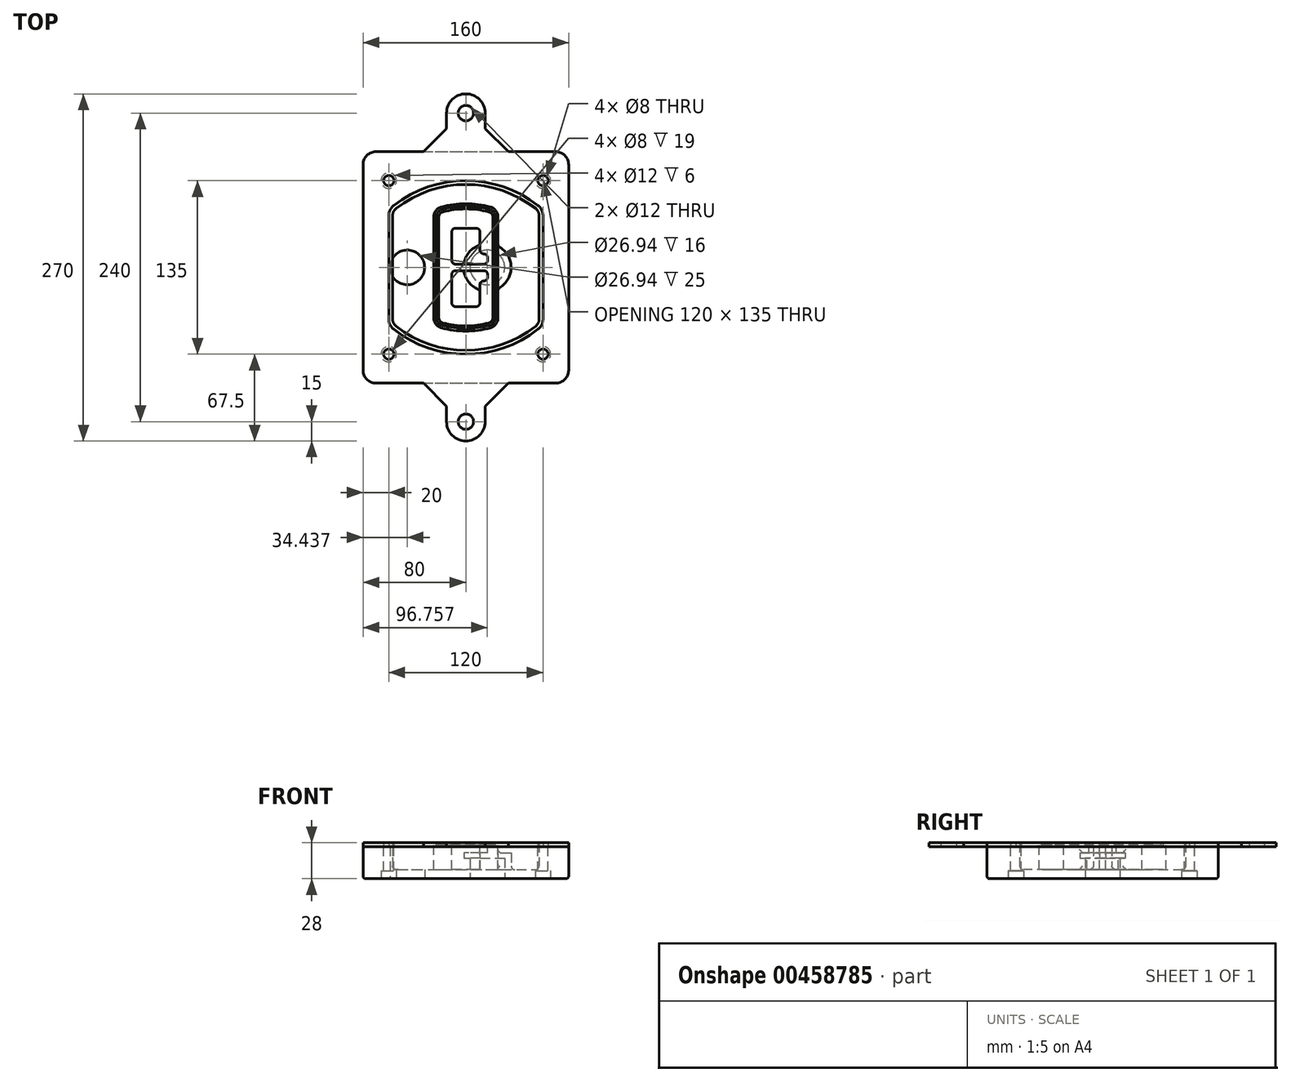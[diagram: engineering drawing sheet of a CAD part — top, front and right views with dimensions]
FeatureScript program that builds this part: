
annotation { "Feature Type Name" : "Feature", "Feature Type Description" : "" }
export const myFeature = defineFeature(function(context is Context, id is Id, definition is map)
    precondition{}
    {
        {
            var Q0;
            Q0=qCreatedBy(makeId("Top.planeOp"),FACE);
            var sketch = newSketch(context, id + "F0", { "sketchPlane" : qUnion([Q0])});
            skPoint(sketch, "E0.rect.middle", {"position": v(0, 0) * mm});
            skLineSegment(sketch, "E1.bottom", {"start": v(-70, -90) * mm, "end": v(70, -90) * mm});
            skLineSegment(sketch, "E1.top", {"start": v(-70, 90) * mm, "end": v(70, 90) * mm});
            skLineSegment(sketch, "E1.left", {"start": v(-80, -80) * mm, "end": v(-80, 80) * mm});
            skLineSegment(sketch, "E1.right", {"start": v(80, -80) * mm, "end": v(80, 80) * mm});
            skLineSegment(sketch, "E2", {"start": v(-80, 90) * mm, "end": v(80, -90) * mm, "construction": true});
            skLineSegment(sketch, "E3", {"start": v(80, 90) * mm, "end": v(-80, -90) * mm, "construction": true});
            skCircle(sketch, "E4", {"center": v(-60, 67.5) * mm, "radius": 4 * mm});
            skCircle(sketch, "E5", {"center": v(60, 67.5) * mm, "radius": 4 * mm});
            skCircle(sketch, "E6", {"center": v(60, -67.5) * mm, "radius": 4 * mm});
            skCircle(sketch, "E7", {"center": v(-60, -67.5) * mm, "radius": 4 * mm});
            skLineSegment(sketch, "E8", {"start": v(-60, 67.5) * mm, "end": v(60, 67.5) * mm, "construction": true});
            skLineSegment(sketch, "E9", {"start": v(60, 67.5) * mm, "end": v(60, -67.5) * mm, "construction": true});
            skLineSegment(sketch, "E10", {"start": v(60, -67.5) * mm, "end": v(-60, -67.5) * mm, "construction": true});
            skLineSegment(sketch, "E11", {"start": v(-60, -67.5) * mm, "end": v(-60, 67.5) * mm, "construction": true});
            skLineSegment(sketch, "E12", {"start": v(-60, 40.3) * mm, "end": v(-60, -40.3) * mm});
            skLineSegment(sketch, "E13", {"start": v(60, 40.3) * mm, "end": v(60, -40.3) * mm});
            skArc(sketch, "E14", {"start": v(56.15, 48.18) * mm, "mid": v(0, 67.5) * mm, "end": v(-56.15, 48.18) * mm});
            skArc(sketch, "E15", {"start": v(-56.15, -48.18) * mm, "mid": v(0, -67.5) * mm, "end": v(56.15, -48.18) * mm});
            skLineSegment(sketch, "E16", {"start": v(-60, 0) * mm, "end": v(60, 0) * mm, "construction": true});
            skPoint(sketch, "E17.visualSharp", {"position": v(-60, -45) * mm});
            skArc(sketch, "E17.filletArc", {"start": v(-60, -40.3) * mm, "mid": v(-58.99, -44.68) * mm, "end": v(-56.15, -48.18) * mm});
            skPoint(sketch, "E18.visualSharp", {"position": v(-60, 45) * mm});
            skArc(sketch, "E18.filletArc", {"start": v(-56.15, 48.18) * mm, "mid": v(-58.99, 44.68) * mm, "end": v(-60, 40.3) * mm});
            skPoint(sketch, "E19.visualSharp", {"position": v(60, 45) * mm});
            skArc(sketch, "E19.filletArc", {"start": v(60, 40.3) * mm, "mid": v(58.99, 44.68) * mm, "end": v(56.15, 48.18) * mm});
            skPoint(sketch, "E20.visualSharp", {"position": v(60, -45) * mm});
            skArc(sketch, "E20.filletArc", {"start": v(56.15, -48.18) * mm, "mid": v(58.99, -44.68) * mm, "end": v(60, -40.3) * mm});
            skPoint(sketch, "E21.visualSharp", {"position": v(-80, 90) * mm});
            skArc(sketch, "E21.filletArc", {"start": v(-70, 90) * mm, "mid": v(-77.07, 87.07) * mm, "end": v(-80, 80) * mm});
            skPoint(sketch, "E22.visualSharp", {"position": v(80, 90) * mm});
            skArc(sketch, "E22.filletArc", {"start": v(80, 80) * mm, "mid": v(77.07, 87.07) * mm, "end": v(70, 90) * mm});
            skPoint(sketch, "E23.visualSharp", {"position": v(80, -90) * mm});
            skArc(sketch, "E23.filletArc", {"start": v(70, -90) * mm, "mid": v(77.07, -87.07) * mm, "end": v(80, -80) * mm});
            skPoint(sketch, "E24.visualSharp", {"position": v(-80, -90) * mm});
            skArc(sketch, "E24.filletArc", {"start": v(-80, -80) * mm, "mid": v(-77.07, -87.07) * mm, "end": v(-70, -90) * mm});
            skArc(sketch, "E25.0", {"start": v(57, 40.3) * mm, "mid": v(56.3, 43.36) * mm, "end": v(54.3, 45.81) * mm});
            skLineSegment(sketch, "E25.1", {"start": v(57, 40.3) * mm, "end": v(57, -40.3) * mm});
            skArc(sketch, "E25.2", {"start": v(54.3, -45.81) * mm, "mid": v(56.3, -43.36) * mm, "end": v(57, -40.3) * mm});
            skArc(sketch, "E25.3", {"start": v(-54.3, -45.81) * mm, "mid": v(0, -64.5) * mm, "end": v(54.3, -45.81) * mm});
            skArc(sketch, "E25.4", {"start": v(-57, -40.3) * mm, "mid": v(-56.3, -43.36) * mm, "end": v(-54.3, -45.81) * mm});
            skArc(sketch, "E25.5", {"start": v(54.3, 45.81) * mm, "mid": v(0, 64.5) * mm, "end": v(-54.3, 45.81) * mm});
            skLineSegment(sketch, "E25.6", {"start": v(-57, 40.3) * mm, "end": v(-57, -40.3) * mm});
            skArc(sketch, "E25.7", {"start": v(-54.3, 45.81) * mm, "mid": v(-56.3, 43.36) * mm, "end": v(-57, 40.3) * mm});
            skArc(sketch, "E26.0", {"start": v(-58.62, 51.33) * mm, "mid": v(-62.58, 46.43) * mm, "end": v(-64, 40.3) * mm});
            skArc(sketch, "E26.1", {"start": v(58.62, 51.33) * mm, "mid": v(0, 71.5) * mm, "end": v(-58.62, 51.33) * mm});
            skArc(sketch, "E26.2", {"start": v(64, 40.3) * mm, "mid": v(62.58, 46.43) * mm, "end": v(58.62, 51.33) * mm});
            skLineSegment(sketch, "E26.3", {"start": v(64, 40.3) * mm, "end": v(64, -40.3) * mm});
            skArc(sketch, "E26.4", {"start": v(58.62, -51.33) * mm, "mid": v(62.58, -46.43) * mm, "end": v(64, -40.3) * mm});
            skLineSegment(sketch, "E26.5", {"start": v(-64, 40.3) * mm, "end": v(-64, -40.3) * mm});
            skArc(sketch, "E26.6", {"start": v(-58.62, -51.33) * mm, "mid": v(0, -71.5) * mm, "end": v(58.62, -51.33) * mm});
            skArc(sketch, "E26.7", {"start": v(-64, -40.3) * mm, "mid": v(-62.58, -46.43) * mm, "end": v(-58.62, -51.33) * mm});
            skSolve(sketch);
        }
        {
            var Q0;
            Q0=makeQuery(id+"F0.imprint","IMPRINT",FACE,{"disambiguationData":[TD([[makeQuery(id+"F0.imprint","IMPRINT",EDGE,{"derivedFrom":sQuery(id+"F0.wireOp",EDGE,"E1.bottom")}),1.0]])]});
            var Q1;
            Q1=makeQuery(id+"F0.imprint","IMPRINT",FACE,{"disambiguationData":[TD([[makeQuery(id+"F0.imprint","IMPRINT",EDGE,{"derivedFrom":sQuery(id+"F0.wireOp",EDGE,"E12")}),1.0]])]});
            var Q2;
            Q2=makeQuery(id+"F0.imprint","IMPRINT",FACE,{"disambiguationData":[TD([[makeQuery(id+"F0.imprint","IMPRINT",EDGE,{"derivedFrom":sQuery(id+"F0.wireOp",EDGE,"E25.0")}),1.0]])]});
            var Q3;
            Q3=makeQuery(id+"F0.imprint","IMPRINT",FACE,{"disambiguationData":[TD([[makeQuery(id+"F0.imprint","IMPRINT",EDGE,{"derivedFrom":sQuery(id+"F0.wireOp",EDGE,"E12")}),-1.0]])]});
            extrude(context, id + "F1", {"entities" : qUnion([Q0, Q1, Q2, Q3]), "oppositeDirection" : true, "depth" : 25 * mm});
        }
        {
            var Q0;
            Q0=makeQuery(id+"F0.imprint","IMPRINT",FACE,{"disambiguationData":[TD([[makeQuery(id+"F0.imprint","IMPRINT",EDGE,{"derivedFrom":sQuery(id+"F0.wireOp",EDGE,"E12")}),1.0]])]});
            extrude(context, id + "F2", {"entities" : qUnion([Q0]), "operationType" : NewBodyOperationType.ADD, "depth" : 3 * mm});
        }
        {
            var Q0;
            Q0=makeQuery(id+"F0.imprint","IMPRINT",FACE,{"disambiguationData":[TD([[makeQuery(id+"F0.imprint","IMPRINT",EDGE,{"derivedFrom":sQuery(id+"F0.wireOp",EDGE,"E25.0")}),1.0]])]});
            extrude(context, id + "F3", {"entities" : qUnion([Q0]), "operationType" : NewBodyOperationType.REMOVE, "oppositeDirection" : true, "depth" : 18 * mm});
        }
        {
            var Q0;
            Q0=makeQuery(id+"F2.opExtrude","CAP_FACE",FACE,{"disambiguationData":[OSD([sQuery(id+"F0.wireOp",EDGE,"E12"),sQuery(id+"F0.wireOp",EDGE,"E13"),sQuery(id+"F0.wireOp",EDGE,"E14"),sQuery(id+"F0.wireOp",EDGE,"E15"),sQuery(id+"F0.wireOp",EDGE,"E17.filletArc"),sQuery(id+"F0.wireOp",EDGE,"E18.filletArc"),sQuery(id+"F0.wireOp",EDGE,"E19.filletArc"),sQuery(id+"F0.wireOp",EDGE,"E20.filletArc"),sQuery(id+"F0.wireOp",EDGE,"E25.0"),sQuery(id+"F0.wireOp",EDGE,"E25.1"),sQuery(id+"F0.wireOp",EDGE,"E25.2"),sQuery(id+"F0.wireOp",EDGE,"E25.3"),sQuery(id+"F0.wireOp",EDGE,"E25.4"),sQuery(id+"F0.wireOp",EDGE,"E25.5"),sQuery(id+"F0.wireOp",EDGE,"E25.6"),sQuery(id+"F0.wireOp",EDGE,"E25.7")])],"isStart":false});
            var sketch = newSketch(context, id + "F4", { "sketchPlane" : qUnion([Q0])});
            skArc(sketch, "E27.0", {"start": v(-19.08, -46.97) * mm, "mid": v(0, -49.5) * mm, "end": v(19.08, -46.97) * mm});
            skArc(sketch, "E28.0", {"start": v(19.08, 46.97) * mm, "mid": v(0, 49.5) * mm, "end": v(-19.08, 46.97) * mm});
            skLineSegment(sketch, "E29", {"start": v(-25, 39.25) * mm, "end": v(-25, -39.25) * mm});
            skLineSegment(sketch, "E30", {"start": v(25, 39.25) * mm, "end": v(25, -39.25) * mm});
            skLineSegment(sketch, "E31", {"start": v(-25, 45.1) * mm, "end": v(25, 45.1) * mm, "construction": true});
            skLineSegment(sketch, "E32", {"start": v(-25, -45.1) * mm, "end": v(25, -45.1) * mm, "construction": true});
            skPoint(sketch, "E33.visualSharp", {"position": v(-25, 45.1) * mm});
            skArc(sketch, "E33.filletArc", {"start": v(-19.08, 46.97) * mm, "mid": v(-23.35, 44.11) * mm, "end": v(-25, 39.25) * mm});
            skPoint(sketch, "E34.visualSharp", {"position": v(25, 45.1) * mm});
            skArc(sketch, "E34.filletArc", {"start": v(25, 39.25) * mm, "mid": v(23.35, 44.11) * mm, "end": v(19.08, 46.97) * mm});
            skPoint(sketch, "E35.visualSharp", {"position": v(25, -45.1) * mm});
            skArc(sketch, "E35.filletArc", {"start": v(19.08, -46.97) * mm, "mid": v(23.35, -44.11) * mm, "end": v(25, -39.25) * mm});
            skPoint(sketch, "E36.visualSharp", {"position": v(-25, -45.1) * mm});
            skArc(sketch, "E36.filletArc", {"start": v(-25, -39.25) * mm, "mid": v(-23.35, -44.11) * mm, "end": v(-19.08, -46.97) * mm});
            skArc(sketch, "E37.0", {"start": v(54.3, 45.81) * mm, "mid": v(0, 64.5) * mm, "end": v(-54.3, 45.81) * mm});
            skArc(sketch, "E37.1", {"start": v(-54.3, 45.81) * mm, "mid": v(-56.3, 43.36) * mm, "end": v(-57, 40.3) * mm});
            skLineSegment(sketch, "E37.2", {"start": v(-57, 40.3) * mm, "end": v(-57, -40.3) * mm});
            skArc(sketch, "E37.3", {"start": v(-57, -40.3) * mm, "mid": v(-56.3, -43.36) * mm, "end": v(-54.3, -45.81) * mm});
            skArc(sketch, "E37.4", {"start": v(-54.3, -45.81) * mm, "mid": v(0, -64.5) * mm, "end": v(54.3, -45.81) * mm});
            skArc(sketch, "E37.5", {"start": v(54.3, -45.81) * mm, "mid": v(56.3, -43.36) * mm, "end": v(57, -40.3) * mm});
            skLineSegment(sketch, "E37.6", {"start": v(57, 40.3) * mm, "end": v(57, -40.3) * mm});
            skArc(sketch, "E37.7", {"start": v(57, 40.3) * mm, "mid": v(56.3, 43.36) * mm, "end": v(54.3, 45.81) * mm});
            skLineSegment(sketch, "E38.0", {"start": v(23, 39.25) * mm, "end": v(23, -39.25) * mm});
            skArc(sketch, "E38.1", {"start": v(18.56, -45.04) * mm, "mid": v(21.76, -42.9) * mm, "end": v(23, -39.25) * mm});
            skArc(sketch, "E38.2", {"start": v(-18.56, -45.04) * mm, "mid": v(0, -47.5) * mm, "end": v(18.56, -45.04) * mm});
            skArc(sketch, "E38.3", {"start": v(-23, -39.25) * mm, "mid": v(-21.76, -42.9) * mm, "end": v(-18.56, -45.04) * mm});
            skLineSegment(sketch, "E38.4", {"start": v(-23, 39.25) * mm, "end": v(-23, -39.25) * mm});
            skArc(sketch, "E38.5", {"start": v(23, 39.25) * mm, "mid": v(21.76, 42.9) * mm, "end": v(18.56, 45.04) * mm});
            skArc(sketch, "E38.6", {"start": v(-18.56, 45.04) * mm, "mid": v(-21.76, 42.9) * mm, "end": v(-23, 39.25) * mm});
            skArc(sketch, "E38.7", {"start": v(18.56, 45.04) * mm, "mid": v(0, 47.5) * mm, "end": v(-18.56, 45.04) * mm});
            skArc(sketch, "E39.0", {"start": v(21, 39.25) * mm, "mid": v(20.18, 41.68) * mm, "end": v(18.04, 43.1) * mm});
            skLineSegment(sketch, "E39.1", {"start": v(21, 39.25) * mm, "end": v(21, -39.25) * mm});
            skArc(sketch, "E39.2", {"start": v(18.04, -43.1) * mm, "mid": v(20.18, -41.68) * mm, "end": v(21, -39.25) * mm});
            skArc(sketch, "E39.3", {"start": v(-18.04, -43.1) * mm, "mid": v(0, -45.5) * mm, "end": v(18.04, -43.1) * mm});
            skArc(sketch, "E39.4", {"start": v(-21, -39.25) * mm, "mid": v(-20.18, -41.68) * mm, "end": v(-18.04, -43.1) * mm});
            skArc(sketch, "E39.5", {"start": v(18.04, 43.1) * mm, "mid": v(0, 45.5) * mm, "end": v(-18.04, 43.1) * mm});
            skLineSegment(sketch, "E39.6", {"start": v(-21, 39.25) * mm, "end": v(-21, -39.25) * mm});
            skArc(sketch, "E39.7", {"start": v(-18.04, 43.1) * mm, "mid": v(-20.18, 41.68) * mm, "end": v(-21, 39.25) * mm});
            skLineSegment(sketch, "E40", {"start": v(-25, 0) * mm, "end": v(25, 0) * mm, "construction": true});
            skLineSegment(sketch, "E41", {"start": v(-11, 5.5) * mm, "end": v(-11, 27.5) * mm});
            skLineSegment(sketch, "E42", {"start": v(-8, 30.5) * mm, "end": v(8, 30.5) * mm});
            skLineSegment(sketch, "E43", {"start": v(11, 27.5) * mm, "end": v(11, 13.5) * mm});
            skLineSegment(sketch, "E44", {"start": v(14, 10.5) * mm, "end": v(14, 10.5) * mm});
            skLineSegment(sketch, "E45", {"start": v(17, 7.5) * mm, "end": v(17, 5.5) * mm});
            skLineSegment(sketch, "E46", {"start": v(14, 2.5) * mm, "end": v(-8, 2.5) * mm});
            skPoint(sketch, "E47.visualSharp", {"position": v(-11, 30.5) * mm});
            skArc(sketch, "E47.filletArc", {"start": v(-8, 30.5) * mm, "mid": v(-10.12, 29.62) * mm, "end": v(-11, 27.5) * mm});
            skPoint(sketch, "E48.visualSharp", {"position": v(11, 30.5) * mm});
            skArc(sketch, "E48.filletArc", {"start": v(11, 27.5) * mm, "mid": v(10.12, 29.62) * mm, "end": v(8, 30.5) * mm});
            skPoint(sketch, "E49.visualSharp", {"position": v(11, 10.5) * mm});
            skArc(sketch, "E49.filletArc", {"start": v(11, 13.5) * mm, "mid": v(11.88, 11.38) * mm, "end": v(14, 10.5) * mm});
            skPoint(sketch, "E50.visualSharp", {"position": v(17, 10.5) * mm});
            skArc(sketch, "E50.filletArc", {"start": v(17, 7.5) * mm, "mid": v(16.12, 9.62) * mm, "end": v(14, 10.5) * mm});
            skPoint(sketch, "E51.visualSharp", {"position": v(17, 2.5) * mm});
            skArc(sketch, "E51.filletArc", {"start": v(14, 2.5) * mm, "mid": v(16.12, 3.38) * mm, "end": v(17, 5.5) * mm});
            skPoint(sketch, "E52.visualSharp", {"position": v(-11, 2.5) * mm});
            skArc(sketch, "E52.filletArc", {"start": v(-11, 5.5) * mm, "mid": v(-10.12, 3.38) * mm, "end": v(-8, 2.5) * mm});
            skLineSegment(sketch, "E53.0.MirrorCS", {"start": v(14, -2.5) * mm, "end": v(-8, -2.5) * mm});
            skArc(sketch, "E54.0.MirrorCS", {"start": v(-11, -5.5) * mm, "mid": v(-10.12, -3.38) * mm, "end": v(-8, -2.5) * mm});
            skLineSegment(sketch, "E55.0.MirrorCS", {"start": v(-11, -5.5) * mm, "end": v(-11, -27.5) * mm});
            skArc(sketch, "E56.0.MirrorCS", {"start": v(-8, -30.5) * mm, "mid": v(-10.12, -29.62) * mm, "end": v(-11, -27.5) * mm});
            skLineSegment(sketch, "E57.0.MirrorCS", {"start": v(-8, -30.5) * mm, "end": v(8, -30.5) * mm});
            skArc(sketch, "E58.0.MirrorCS", {"start": v(11, -27.5) * mm, "mid": v(10.12, -29.62) * mm, "end": v(8, -30.5) * mm});
            skLineSegment(sketch, "E59.0.MirrorCS", {"start": v(11, -27.5) * mm, "end": v(11, -13.5) * mm});
            skArc(sketch, "E60.0.MirrorCS", {"start": v(11, -13.5) * mm, "mid": v(11.88, -11.38) * mm, "end": v(14, -10.5) * mm});
            skArc(sketch, "E61.0.MirrorCS", {"start": v(17, -7.5) * mm, "mid": v(16.12, -9.62) * mm, "end": v(14, -10.5) * mm});
            skLineSegment(sketch, "E62.0.MirrorCS", {"start": v(17, -7.5) * mm, "end": v(17, -5.5) * mm});
            skArc(sketch, "E63.0.MirrorCS", {"start": v(14, -2.5) * mm, "mid": v(16.12, -3.38) * mm, "end": v(17, -5.5) * mm});
            skSolve(sketch);
        }
        {
            var Q0;
            Q0=makeQuery(id+"F4.imprint","IMPRINT",FACE,{"disambiguationData":[TD([[makeQuery(id+"F4.imprint","IMPRINT",EDGE,{"derivedFrom":sQuery(id+"F4.wireOp",EDGE,"E27.0")}),1.0]])]});
            var Q1;
            Q1=makeQuery(id+"F4.imprint","IMPRINT",FACE,{"disambiguationData":[TD([[makeQuery(id+"F4.imprint","IMPRINT",EDGE,{"derivedFrom":sQuery(id+"F4.wireOp",EDGE,"E38.0")}),-1.0]])]});
            var Q2;
            Q2=makeQuery(id+"F4.imprint","IMPRINT",FACE,{"disambiguationData":[TD([[makeQuery(id+"F4.imprint","IMPRINT",EDGE,{"derivedFrom":sQuery(id+"F4.wireOp",EDGE,"E39.0")}),1.0]])]});
            extrude(context, id + "F5", {"entities" : qUnion([Q0, Q1, Q2]), "operationType" : NewBodyOperationType.ADD, "endBound" : BoundingType.UP_TO_NEXT, "oppositeDirection" : true, "depth" : 25 * mm});
        }
        {
            var Q0;
            Q0=makeQuery(id+"F4.imprint","IMPRINT",FACE,{"disambiguationData":[TD([[makeQuery(id+"F4.imprint","IMPRINT",EDGE,{"derivedFrom":sQuery(id+"F4.wireOp",EDGE,"E38.0")}),-1.0]])]});
            extrude(context, id + "F6", {"entities" : qUnion([Q0]), "operationType" : NewBodyOperationType.REMOVE, "oppositeDirection" : true, "depth" : 2 * mm});
        }
        {
            var Q0;
            Q0=makeQuery(id+"F1.opExtrude","CAP_FACE",FACE,{"disambiguationData":[OSD([sQuery(id+"F0.wireOp",EDGE,"E1.bottom"),sQuery(id+"F0.wireOp",EDGE,"E1.top"),sQuery(id+"F0.wireOp",EDGE,"E1.left"),sQuery(id+"F0.wireOp",EDGE,"E1.right"),sQuery(id+"F0.wireOp",EDGE,"E4"),sQuery(id+"F0.wireOp",EDGE,"E5"),sQuery(id+"F0.wireOp",EDGE,"E6"),sQuery(id+"F0.wireOp",EDGE,"E7"),sQuery(id+"F0.wireOp",EDGE,"E21.filletArc"),sQuery(id+"F0.wireOp",EDGE,"E22.filletArc"),sQuery(id+"F0.wireOp",EDGE,"E23.filletArc"),sQuery(id+"F0.wireOp",EDGE,"E24.filletArc")])],"isStart":false});
            var sketch = newSketch(context, id + "F7", { "sketchPlane" : qUnion([Q0])});
            skCircle(sketch, "E64", {"center": v(16.76, 0) * mm, "radius": 13.47 * mm});
            skCircle(sketch, "E65", {"center": v(-45.56, 0) * mm, "radius": 13.47 * mm});
            skLineSegment(sketch, "E66", {"start": v(80, 0) * mm, "end": v(-80, 0) * mm});
            skCircle(sketch, "E67", {"center": v(16.76, 0) * mm, "radius": 18.47 * mm});
            skCircle(sketch, "E68", {"center": v(60, -67.5) * mm, "radius": 6 * mm});
            skCircle(sketch, "E69", {"center": v(-60, -67.5) * mm, "radius": 6 * mm});
            skCircle(sketch, "E70", {"center": v(-60, 67.5) * mm, "radius": 6 * mm});
            skCircle(sketch, "E71", {"center": v(60, 67.5) * mm, "radius": 6 * mm});
            skSolve(sketch);
        }
        {
            var Q0;
            {var subQ1=sQuery(id+"F7.wireOp",EDGE,"E66");var subQ4=sQuery(id+"F7.wireOp",EDGE,"E64");var subQ6=makeQuery(id+"F7.imprint","INTERSECT",VERTEX,{"disambiguationData":[OD(0.0)],"derivedFrom":[subQ4,subQ1]});Q0=makeQuery(id+"F7.imprint","IMPRINT",FACE,{"disambiguationData":[TD([[makeQuery(id+"F7.imprint","IMPRINT",EDGE,{"disambiguationData":[TD([[subQ6,-1.0]])],"derivedFrom":subQ4}),-1.0]])]});}
            var Q1;
            {var subQ0=sQuery(id+"F7.wireOp",EDGE,"E66");var subQ1=sQuery(id+"F7.wireOp",EDGE,"E64");var subQ3=makeQuery(id+"F7.imprint","INTERSECT",VERTEX,{"disambiguationData":[OD(0.0)],"derivedFrom":[subQ1,subQ0]});Q1=makeQuery(id+"F7.imprint","IMPRINT",FACE,{"disambiguationData":[TD([[makeQuery(id+"F7.imprint","IMPRINT",EDGE,{"disambiguationData":[TD([[subQ3,-1.0]])],"derivedFrom":subQ1}),1.0]])]});}
            var Q2;
            {var subQ0=sQuery(id+"F7.wireOp",EDGE,"E66");var subQ1=sQuery(id+"F7.wireOp",EDGE,"E64");var subQ3=makeQuery(id+"F7.imprint","INTERSECT",VERTEX,{"disambiguationData":[OD(0.0)],"derivedFrom":[subQ1,subQ0]});Q2=makeQuery(id+"F7.imprint","IMPRINT",FACE,{"disambiguationData":[TD([[makeQuery(id+"F7.imprint","IMPRINT",EDGE,{"disambiguationData":[TD([[subQ3,1.0]])],"derivedFrom":subQ1}),1.0]])]});}
            var Q3;
            {var subQ1=sQuery(id+"F7.wireOp",EDGE,"E66");var subQ4=sQuery(id+"F7.wireOp",EDGE,"E64");var subQ6=makeQuery(id+"F7.imprint","INTERSECT",VERTEX,{"disambiguationData":[OD(0.0)],"derivedFrom":[subQ4,subQ1]});Q3=makeQuery(id+"F7.imprint","IMPRINT",FACE,{"disambiguationData":[TD([[makeQuery(id+"F7.imprint","IMPRINT",EDGE,{"disambiguationData":[TD([[subQ6,1.0]])],"derivedFrom":subQ4}),-1.0]])]});}
            extrude(context, id + "F8", {"entities" : qUnion([Q0, Q1, Q2, Q3]), "operationType" : NewBodyOperationType.ADD, "oppositeDirection" : true, "depth" : 20 * mm});
        }
        {
            var Q0;
            {var subQ0=sQuery(id+"F7.wireOp",EDGE,"E66");var subQ1=sQuery(id+"F7.wireOp",EDGE,"E64");var subQ3=makeQuery(id+"F7.imprint","INTERSECT",VERTEX,{"disambiguationData":[OD(0.0)],"derivedFrom":[subQ1,subQ0]});Q0=makeQuery(id+"F7.imprint","IMPRINT",FACE,{"disambiguationData":[TD([[makeQuery(id+"F7.imprint","IMPRINT",EDGE,{"disambiguationData":[TD([[subQ3,-1.0]])],"derivedFrom":subQ1}),1.0]])]});}
            var Q1;
            {var subQ0=sQuery(id+"F7.wireOp",EDGE,"E66");var subQ1=sQuery(id+"F7.wireOp",EDGE,"E64");var subQ3=makeQuery(id+"F7.imprint","INTERSECT",VERTEX,{"disambiguationData":[OD(0.0)],"derivedFrom":[subQ1,subQ0]});Q1=makeQuery(id+"F7.imprint","IMPRINT",FACE,{"disambiguationData":[TD([[makeQuery(id+"F7.imprint","IMPRINT",EDGE,{"disambiguationData":[TD([[subQ3,1.0]])],"derivedFrom":subQ1}),1.0]])]});}
            extrude(context, id + "F9", {"entities" : qUnion([Q0, Q1]), "operationType" : NewBodyOperationType.REMOVE, "oppositeDirection" : true, "depth" : 16 * mm});
        }
        {
            var Q0;
            {var subQ0=sQuery(id+"F7.wireOp",EDGE,"E66");var subQ1=sQuery(id+"F7.wireOp",EDGE,"E65");var subQ3=makeQuery(id+"F7.imprint","INTERSECT",VERTEX,{"disambiguationData":[OD(0.0)],"derivedFrom":[subQ1,subQ0]});Q0=makeQuery(id+"F7.imprint","IMPRINT",FACE,{"disambiguationData":[TD([[makeQuery(id+"F7.imprint","IMPRINT",EDGE,{"disambiguationData":[TD([[subQ3,-1.0]])],"derivedFrom":subQ1}),1.0]])]});}
            var Q1;
            {var subQ0=sQuery(id+"F7.wireOp",EDGE,"E66");var subQ1=sQuery(id+"F7.wireOp",EDGE,"E65");var subQ3=makeQuery(id+"F7.imprint","INTERSECT",VERTEX,{"disambiguationData":[OD(0.0)],"derivedFrom":[subQ1,subQ0]});Q1=makeQuery(id+"F7.imprint","IMPRINT",FACE,{"disambiguationData":[TD([[makeQuery(id+"F7.imprint","IMPRINT",EDGE,{"disambiguationData":[TD([[subQ3,1.0]])],"derivedFrom":subQ1}),1.0]])]});}
            extrude(context, id + "F10", {"entities" : qUnion([Q0, Q1]), "operationType" : NewBodyOperationType.REMOVE, "oppositeDirection" : true, "depth" : 25 * mm});
        }
        {
            var Q0;
            Q0=makeQuery(id+"F7.imprint","IMPRINT",FACE,{"disambiguationData":[TD([[makeQuery(id+"F7.imprint","IMPRINT",EDGE,{"derivedFrom":sQuery(id+"F7.wireOp",EDGE,"E68")}),1.0]])]});
            var Q1;
            Q1=makeQuery(id+"F7.imprint","IMPRINT",FACE,{"disambiguationData":[TD([[makeQuery(id+"F7.imprint","IMPRINT",EDGE,{"derivedFrom":makeQuery(id+"F1.opExtrude","CAP_EDGE",EDGE,{"disambiguationData":[OSD([sQuery(id+"F0.wireOp",EDGE,"E5")])],"isStart":false})}),-1.0]])]});
            var Q2;
            Q2=makeQuery(id+"F7.imprint","IMPRINT",FACE,{"disambiguationData":[TD([[makeQuery(id+"F7.imprint","IMPRINT",EDGE,{"derivedFrom":sQuery(id+"F7.wireOp",EDGE,"E69")}),1.0]])]});
            var Q3;
            Q3=makeQuery(id+"F7.imprint","IMPRINT",FACE,{"disambiguationData":[TD([[makeQuery(id+"F7.imprint","IMPRINT",EDGE,{"derivedFrom":makeQuery(id+"F1.opExtrude","CAP_EDGE",EDGE,{"disambiguationData":[OSD([sQuery(id+"F0.wireOp",EDGE,"E4")])],"isStart":false})}),-1.0]])]});
            var Q4;
            Q4=makeQuery(id+"F7.imprint","IMPRINT",FACE,{"disambiguationData":[TD([[makeQuery(id+"F7.imprint","IMPRINT",EDGE,{"derivedFrom":sQuery(id+"F7.wireOp",EDGE,"E70")}),1.0]])]});
            var Q5;
            Q5=makeQuery(id+"F7.imprint","IMPRINT",FACE,{"disambiguationData":[TD([[makeQuery(id+"F7.imprint","IMPRINT",EDGE,{"derivedFrom":makeQuery(id+"F1.opExtrude","CAP_EDGE",EDGE,{"disambiguationData":[OSD([sQuery(id+"F0.wireOp",EDGE,"E7")])],"isStart":false})}),-1.0]])]});
            var Q6;
            Q6=makeQuery(id+"F7.imprint","IMPRINT",FACE,{"disambiguationData":[TD([[makeQuery(id+"F7.imprint","IMPRINT",EDGE,{"derivedFrom":sQuery(id+"F7.wireOp",EDGE,"E71")}),1.0]])]});
            var Q7;
            Q7=makeQuery(id+"F7.imprint","IMPRINT",FACE,{"disambiguationData":[TD([[makeQuery(id+"F7.imprint","IMPRINT",EDGE,{"derivedFrom":makeQuery(id+"F1.opExtrude","CAP_EDGE",EDGE,{"disambiguationData":[OSD([sQuery(id+"F0.wireOp",EDGE,"E6")])],"isStart":false})}),-1.0]])]});
            extrude(context, id + "F11", {"entities" : qUnion([Q0, Q1, Q2, Q3, Q4, Q5, Q6, Q7]), "operationType" : NewBodyOperationType.REMOVE, "oppositeDirection" : true, "depth" : 6 * mm});
        }
        {
            var Q0;
            Q0=makeQuery(id+"F9.boolean.opBoolean","COPY",FACE,{"derivedFrom":makeQuery(id+"F9.opExtrude","CAP_FACE",FACE,{"disambiguationData":[OSD([sQuery(id+"F7.wireOp",EDGE,"E64")])],"isStart":false})});
            var sketch = newSketch(context, id + "F12", { "sketchPlane" : qUnion([Q0])});
            skArc(sketch, "E72.0", {"start": v(11, 17.55) * mm, "mid": v(2.57, 11.82) * mm, "end": v(-1.54, 2.5) * mm});
            skArc(sketch, "E72.1", {"start": v(-1.54, -2.5) * mm, "mid": v(2.57, -11.82) * mm, "end": v(11, -17.55) * mm});
            skLineSegment(sketch, "E73", {"start": v(-1.54, -2.5) * mm, "end": v(14, -2.5) * mm});
            skLineSegment(sketch, "E74.0", {"start": v(14, 2.5) * mm, "end": v(-1.54, 2.5) * mm});
            skArc(sketch, "E74.1", {"start": v(14, 2.5) * mm, "mid": v(16.12, 3.38) * mm, "end": v(17, 5.5) * mm});
            skLineSegment(sketch, "E74.2", {"start": v(17, 7.5) * mm, "end": v(17, 5.5) * mm});
            skArc(sketch, "E74.3", {"start": v(17, 7.5) * mm, "mid": v(16.12, 9.62) * mm, "end": v(14, 10.5) * mm});
            skArc(sketch, "E74.4", {"start": v(11, 13.5) * mm, "mid": v(11.88, 11.38) * mm, "end": v(14, 10.5) * mm});
            skLineSegment(sketch, "E74.5", {"start": v(11, 17.55) * mm, "end": v(11, 13.5) * mm});
            skLineSegment(sketch, "E74.7", {"start": v(14, -2.5) * mm, "end": v(-1.54, -2.5) * mm});
            skArc(sketch, "E74.8", {"start": v(14, -2.5) * mm, "mid": v(16.12, -3.38) * mm, "end": v(17, -5.5) * mm});
            skLineSegment(sketch, "E74.9", {"start": v(17, -7.5) * mm, "end": v(17, -5.5) * mm});
            skArc(sketch, "E74.10", {"start": v(17, -7.5) * mm, "mid": v(16.12, -9.62) * mm, "end": v(14, -10.5) * mm});
            skArc(sketch, "E74.11", {"start": v(11, -13.5) * mm, "mid": v(11.88, -11.38) * mm, "end": v(14, -10.5) * mm});
            skLineSegment(sketch, "E74.12", {"start": v(11, -17.55) * mm, "end": v(11, -13.5) * mm});
            skPoint(sketch, "E75.orphan", {"position": v(11, -27.5) * mm});
            skPoint(sketch, "E76.orphan", {"position": v(-8, -2.5) * mm});
            skPoint(sketch, "E77.orphan", {"position": v(-8, 2.5) * mm});
            skPoint(sketch, "E78.orphan", {"position": v(11, 27.5) * mm});
            skSolve(sketch);
        }
        {
            var Q0;
            {var subQ7=sQuery(id+"F12.wireOp",EDGE,"E72.0");var subQ14=sQuery(id+"F12.wireOp",EDGE,"E72.1");var subQ16=sQuery(id+"F12.wireOp",EDGE,"E74.1");var subQ18=sQuery(id+"F12.wireOp",EDGE,"E74.8");Q0=qUnion([makeQuery(id+"F12.imprint","IMPRINT",FACE,{"disambiguationData":[TD([[makeQuery(id+"F12.imprint","IMPRINT",EDGE,{"derivedFrom":subQ7}),1.0]])]}),makeQuery(id+"F12.imprint","IMPRINT",FACE,{"disambiguationData":[TD([[makeQuery(id+"F12.imprint","IMPRINT",EDGE,{"derivedFrom":subQ14}),1.0]])]}),makeQuery(id+"F12.imprint","IMPRINT",FACE,{"disambiguationData":[TD([[makeQuery(id+"F12.imprint","IMPRINT",EDGE,{"derivedFrom":subQ16}),1.0]])]}),makeQuery(id+"F12.imprint","IMPRINT",FACE,{"disambiguationData":[TD([[makeQuery(id+"F12.imprint","IMPRINT",EDGE,{"derivedFrom":subQ18}),-1.0]])]})]);}
            var Q1;
            Q1=makeQuery(id+"F5.boolean.opBoolean","SPLIT",FACE,{"disambiguationData":[TD([makeQuery(id+"F5.opExtrude","SWEPT_FACE",FACE,{"disambiguationData":[OSD([sQuery(id+"F4.wireOp",EDGE,"E41")])]})])],"derivedFrom":makeQuery(id+"F3.boolean.opBoolean","COPY",FACE,{"derivedFrom":makeQuery(id+"F3.opExtrude","CAP_FACE",FACE,{"disambiguationData":[OSD([sQuery(id+"F0.wireOp",EDGE,"E25.0"),sQuery(id+"F0.wireOp",EDGE,"E25.1"),sQuery(id+"F0.wireOp",EDGE,"E25.2"),sQuery(id+"F0.wireOp",EDGE,"E25.3"),sQuery(id+"F0.wireOp",EDGE,"E25.4"),sQuery(id+"F0.wireOp",EDGE,"E25.5"),sQuery(id+"F0.wireOp",EDGE,"E25.6"),sQuery(id+"F0.wireOp",EDGE,"E25.7")])],"isStart":false})})});
            extrude(context, id + "F13", {"entities" : qUnion([Q0]), "operationType" : NewBodyOperationType.REMOVE, "endBound" : BoundingType.UP_TO_SURFACE, "endBoundEntityFace" : qUnion([Q1]), "depth" : 25 * mm});
        }
        {
            var Q0;
            Q0=makeQuery(id+"F3.boolean.opBoolean","COPY",EDGE,{"derivedFrom":makeQuery(id+"F3.opExtrude","CAP_EDGE",EDGE,{"disambiguationData":[OSD([sQuery(id+"F0.wireOp",EDGE,"E25.6")])],"isStart":false})});
            var Q1;
            Q1=makeQuery(id+"F8.boolean.opBoolean","INTERSECT",EDGE,{"derivedFrom":[makeQuery(id+"F5.opExtrude","SWEPT_FACE",FACE,{"disambiguationData":[OSD([sQuery(id+"F4.wireOp",EDGE,"E30")])]}),makeQuery(id+"F8.opExtrude","CAP_FACE",FACE,{"disambiguationData":[OSD([sQuery(id+"F7.wireOp",EDGE,"E67")])],"isStart":false})]});
            var Q2;
            Q2=makeQuery(id+"F8.boolean.opBoolean","INTERSECT",EDGE,{"disambiguationData":[OD(1.0)],"derivedFrom":[makeQuery(id+"F5.opExtrude","SWEPT_FACE",FACE,{"disambiguationData":[OSD([sQuery(id+"F4.wireOp",EDGE,"E30")])]}),makeQuery(id+"F8.opExtrude","SWEPT_FACE",FACE,{"disambiguationData":[OSD([sQuery(id+"F7.wireOp",EDGE,"E67")])]})]});
            var Q3;
            {var subQ0=makeQuery(id+"F3.boolean.opBoolean","COPY",FACE,{"derivedFrom":makeQuery(id+"F3.opExtrude","CAP_FACE",FACE,{"disambiguationData":[OSD([sQuery(id+"F0.wireOp",EDGE,"E25.0"),sQuery(id+"F0.wireOp",EDGE,"E25.1"),sQuery(id+"F0.wireOp",EDGE,"E25.2"),sQuery(id+"F0.wireOp",EDGE,"E25.3"),sQuery(id+"F0.wireOp",EDGE,"E25.4"),sQuery(id+"F0.wireOp",EDGE,"E25.5"),sQuery(id+"F0.wireOp",EDGE,"E25.6"),sQuery(id+"F0.wireOp",EDGE,"E25.7")])],"isStart":false})});var subQ1=sQuery(id+"F4.wireOp",EDGE,"E30");Q3=makeQuery(id+"F8.boolean.opBoolean","SPLIT",EDGE,{"disambiguationData":[TD([makeQuery(id+"F5.opExtrude","SWEPT_FACE",FACE,{"disambiguationData":[OSD([sQuery(id+"F4.wireOp",EDGE,"E35.filletArc")])]})])],"derivedFrom":makeQuery(id+"F5.opExtrude","TWEAK_EDGE",EDGE,{"derivedFrom":[subQ0,makeQuery(id+"F4.imprint","IMPRINT",EDGE,{"derivedFrom":subQ1})]})});}
            var Q4;
            {var subQ0=sQuery(id+"F0.wireOp",EDGE,"E25.0");var subQ1=sQuery(id+"F0.wireOp",EDGE,"E25.1");var subQ2=sQuery(id+"F0.wireOp",EDGE,"E25.2");var subQ3=sQuery(id+"F0.wireOp",EDGE,"E25.3");var subQ4=sQuery(id+"F0.wireOp",EDGE,"E25.4");var subQ5=sQuery(id+"F0.wireOp",EDGE,"E25.5");var subQ6=sQuery(id+"F0.wireOp",EDGE,"E25.6");var subQ7=sQuery(id+"F0.wireOp",EDGE,"E25.7");Q4=makeQuery(id+"F8.boolean.opBoolean","INTERSECT",EDGE,{"derivedFrom":[makeQuery(id+"F5.boolean.opBoolean","SPLIT",FACE,{"disambiguationData":[TD([makeQuery(id+"F2.opExtrude","SWEPT_FACE",FACE,{"disambiguationData":[OSD([subQ0])]})])],"derivedFrom":makeQuery(id+"F3.boolean.opBoolean","COPY",FACE,{"derivedFrom":makeQuery(id+"F3.opExtrude","CAP_FACE",FACE,{"disambiguationData":[OSD([subQ0,subQ1,subQ2,subQ3,subQ4,subQ5,subQ6,subQ7])],"isStart":false})})}),makeQuery(id+"F8.opExtrude","SWEPT_FACE",FACE,{"disambiguationData":[OSD([sQuery(id+"F7.wireOp",EDGE,"E67")])]})]});}
            var Q5;
            Q5=makeQuery(id+"F8.boolean.opBoolean","INTERSECT",EDGE,{"disambiguationData":[OD(0.0)],"derivedFrom":[makeQuery(id+"F5.opExtrude","SWEPT_FACE",FACE,{"disambiguationData":[OSD([sQuery(id+"F4.wireOp",EDGE,"E30")])]}),makeQuery(id+"F8.opExtrude","SWEPT_FACE",FACE,{"disambiguationData":[OSD([sQuery(id+"F7.wireOp",EDGE,"E67")])]})]});
            fillet(context, id + "F14", {"entities" : qUnion([Q0, Q1, Q2, Q3, Q4, Q5]), "radius" : 3 * mm, "tangentPropagation" : true, "allowEdgeOverflow" : false});
        }
        {
            var Q0;
            Q0=makeQuery(id+"F1.opExtrude","CAP_EDGE",EDGE,{"disambiguationData":[OSD([sQuery(id+"F0.wireOp",EDGE,"E1.bottom")])],"isStart":false});
            fillet(context, id + "F15", {"entities" : qUnion([Q0]), "radius" : 2 * mm, "tangentPropagation" : true, "allowEdgeOverflow" : false});
        }
        {
            var Q0;
            {var subQ0=sQuery(id+"F0.wireOp",EDGE,"E21.filletArc");var subQ1=sQuery(id+"F0.wireOp",EDGE,"E7");var subQ2=sQuery(id+"F0.wireOp",EDGE,"E6");var subQ3=sQuery(id+"F0.wireOp",EDGE,"E5");var subQ4=sQuery(id+"F0.wireOp",EDGE,"E4");var subQ5=sQuery(id+"F0.wireOp",EDGE,"E22.filletArc");var subQ6=sQuery(id+"F0.wireOp",EDGE,"E1.bottom");var subQ7=sQuery(id+"F0.wireOp",EDGE,"E1.right");var subQ8=sQuery(id+"F0.wireOp",EDGE,"E1.top");var subQ9=sQuery(id+"F0.wireOp",EDGE,"E1.left");var subQ10=sQuery(id+"F0.wireOp",EDGE,"E23.filletArc");var subQ11=sQuery(id+"F0.wireOp",EDGE,"E24.filletArc");Q0=makeQuery(id+"F2.boolean.opBoolean","SPLIT",FACE,{"disambiguationData":[TD([makeQuery(id+"F1.opExtrude","SWEPT_FACE",FACE,{"disambiguationData":[OSD([subQ6])]})])],"derivedFrom":makeQuery(id+"F1.opExtrude","CAP_FACE",FACE,{"disambiguationData":[OSD([subQ6,subQ8,subQ9,subQ7,subQ4,subQ3,subQ2,subQ1,subQ0,subQ5,subQ10,subQ11])],"isStart":true})});}
            var sketch = newSketch(context, id + "F16", { "sketchPlane" : qUnion([Q0])});
            skCircle(sketch, "E79.0", {"center": v(60, 67.5) * mm, "radius": 4 * mm});
            skArc(sketch, "E79.1", {"start": v(80, 80) * mm, "mid": v(77.07, 87.07) * mm, "end": v(70, 90) * mm});
            skLineSegment(sketch, "E79.2", {"start": v(80, -80) * mm, "end": v(80, 80) * mm});
            skArc(sketch, "E79.3", {"start": v(70, -90) * mm, "mid": v(77.07, -87.07) * mm, "end": v(80, -80) * mm});
            skCircle(sketch, "E79.4", {"center": v(60, -67.5) * mm, "radius": 4 * mm});
            skLineSegment(sketch, "E79.5", {"start": v(-70, -90) * mm, "end": v(70, -90) * mm});
            skCircle(sketch, "E79.6", {"center": v(-60, -67.5) * mm, "radius": 4 * mm});
            skArc(sketch, "E79.7", {"start": v(-80, -80) * mm, "mid": v(-77.07, -87.07) * mm, "end": v(-70, -90) * mm});
            skLineSegment(sketch, "E79.8", {"start": v(-80, -80) * mm, "end": v(-80, 80) * mm});
            skArc(sketch, "E79.9", {"start": v(-70, 90) * mm, "mid": v(-77.07, 87.07) * mm, "end": v(-80, 80) * mm});
            skLineSegment(sketch, "E79.10", {"start": v(-70, 90) * mm, "end": v(70, 90) * mm});
            skCircle(sketch, "E79.11", {"center": v(-60, 67.5) * mm, "radius": 4 * mm});
            skArc(sketch, "E79.12", {"start": v(-56.15, -48.18) * mm, "mid": v(0, -67.5) * mm, "end": v(56.15, -48.18) * mm});
            skArc(sketch, "E79.13", {"start": v(56.15, -48.18) * mm, "mid": v(58.99, -44.68) * mm, "end": v(60, -40.3) * mm});
            skLineSegment(sketch, "E79.14", {"start": v(60, 40.3) * mm, "end": v(60, -40.3) * mm});
            skArc(sketch, "E79.15", {"start": v(60, 40.3) * mm, "mid": v(58.99, 44.68) * mm, "end": v(56.15, 48.18) * mm});
            skArc(sketch, "E79.16", {"start": v(56.15, 48.18) * mm, "mid": v(0, 67.5) * mm, "end": v(-56.15, 48.18) * mm});
            skArc(sketch, "E79.17", {"start": v(-56.15, 48.18) * mm, "mid": v(-58.99, 44.68) * mm, "end": v(-60, 40.3) * mm});
            skLineSegment(sketch, "E79.18", {"start": v(-60, 40.3) * mm, "end": v(-60, -40.3) * mm});
            skArc(sketch, "E79.19", {"start": v(-60, -40.3) * mm, "mid": v(-58.99, -44.68) * mm, "end": v(-56.15, -48.18) * mm});
            skCircle(sketch, "E80", {"center": v(0, 120) * mm, "radius": 6 * mm});
            skLineSegment(sketch, "E81", {"start": v(0, 120) * mm, "end": v(0, 90) * mm, "construction": true});
            skLineSegment(sketch, "E82", {"start": v(-15, 108) * mm, "end": v(-15, 120) * mm});
            skArc(sketch, "E83", {"start": v(-15, 120) * mm, "mid": v(0, 135) * mm, "end": v(15, 120) * mm});
            skLineSegment(sketch, "E84", {"start": v(15, 120) * mm, "end": v(15, 108) * mm});
            skLineSegment(sketch, "E85", {"start": v(15, 108) * mm, "end": v(33, 90) * mm});
            skLineSegment(sketch, "E86", {"start": v(-15, 108) * mm, "end": v(-33, 90) * mm});
            skLineSegment(sketch, "E87", {"start": v(-80, 0) * mm, "end": v(80, 0) * mm, "construction": true});
            skCircle(sketch, "E88.MirrorC", {"center": v(0, -120) * mm, "radius": 6 * mm});
            skLineSegment(sketch, "E89.MirrorCS", {"start": v(15, -120) * mm, "end": v(15, -108) * mm});
            skLineSegment(sketch, "E90.MirrorCS", {"start": v(-15, -108) * mm, "end": v(-15, -120) * mm});
            skArc(sketch, "E91.MirrorCS", {"start": v(-15, -120) * mm, "mid": v(0, -135) * mm, "end": v(15, -120) * mm});
            skLineSegment(sketch, "E92.MirrorCS", {"start": v(0, -120) * mm, "end": v(0, -90) * mm, "construction": true});
            skLineSegment(sketch, "E93.MirrorCS", {"start": v(15, -108) * mm, "end": v(33, -90) * mm});
            skLineSegment(sketch, "E94.MirrorCS", {"start": v(-15, -108) * mm, "end": v(-33, -90) * mm});
            skSolve(sketch);
        }
        {
            var Q0;
            Q0 = qSketchRegion(id + "F16", true);
            var Q1;
            Q1=makeQuery(id+"F2.opExtrude","CAP_FACE",FACE,{"disambiguationData":[OSD([sQuery(id+"F0.wireOp",EDGE,"E12"),sQuery(id+"F0.wireOp",EDGE,"E13"),sQuery(id+"F0.wireOp",EDGE,"E14"),sQuery(id+"F0.wireOp",EDGE,"E15"),sQuery(id+"F0.wireOp",EDGE,"E17.filletArc"),sQuery(id+"F0.wireOp",EDGE,"E18.filletArc"),sQuery(id+"F0.wireOp",EDGE,"E19.filletArc"),sQuery(id+"F0.wireOp",EDGE,"E20.filletArc"),sQuery(id+"F0.wireOp",EDGE,"E25.0"),sQuery(id+"F0.wireOp",EDGE,"E25.1"),sQuery(id+"F0.wireOp",EDGE,"E25.2"),sQuery(id+"F0.wireOp",EDGE,"E25.3"),sQuery(id+"F0.wireOp",EDGE,"E25.4"),sQuery(id+"F0.wireOp",EDGE,"E25.5"),sQuery(id+"F0.wireOp",EDGE,"E25.6"),sQuery(id+"F0.wireOp",EDGE,"E25.7")])],"isStart":false});
            extrude(context, id + "F17", {"entities" : qUnion([Q0]), "endBound" : BoundingType.UP_TO_SURFACE, "endBoundEntityFace" : qUnion([Q1]), "depth" : 25 * mm});
        }
    });
